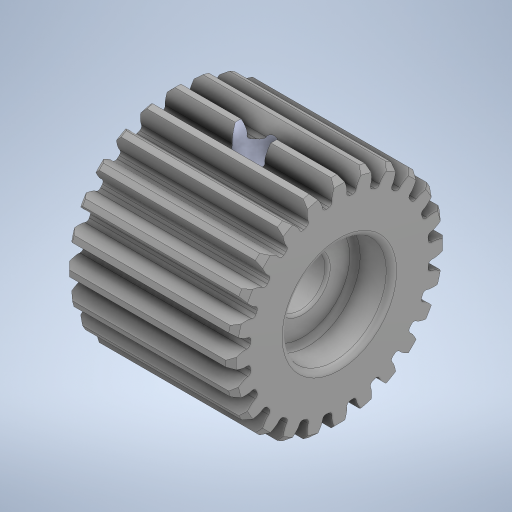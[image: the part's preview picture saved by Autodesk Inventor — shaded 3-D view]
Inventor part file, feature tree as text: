
AUTODESK INVENTOR PART (.ipt)
format: ipt  version: 2023.1 (Build 271208000, 208)  size: 939,520 bytes
history: native  units: mm
features: other x1, fillet x1
ambient origin geometry x8: Origin, YZ Plane, XZ Plane, XY Plane, X Axis, Y Axis, Z Axis, Center Point
bodies: Solid1 (feature_tree)
feature tree (2):
  other  "39300A_TXM-Linear Slide Gear.STEP"
  fillet  "Fillet3"  [1 undecoded]
note: 1 required parameter value undecoded (feature->parameter linkage not recoverable at this tier; creation-order binding heuristic only, values carry confidence <= 0.55)
